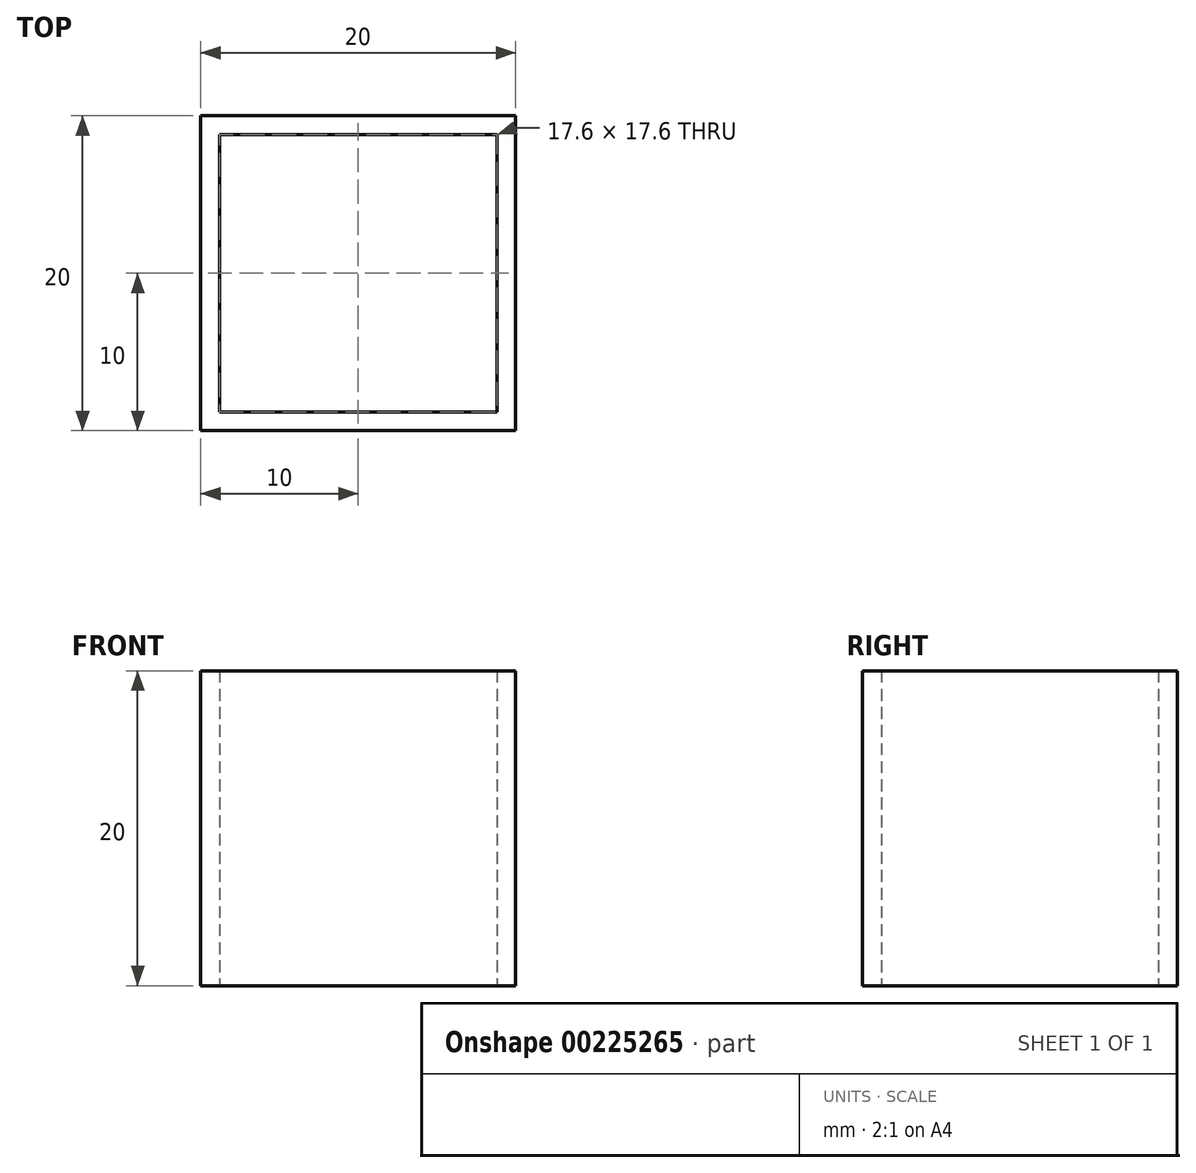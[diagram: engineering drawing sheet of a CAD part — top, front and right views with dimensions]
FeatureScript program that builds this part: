
annotation { "Feature Type Name" : "Feature", "Feature Type Description" : "" }
export const myFeature = defineFeature(function(context is Context, id is Id, definition is map)
    precondition{}
    {
        {
            var Q0;
            Q0=qCreatedBy(makeId("Top.planeOp"),FACE);
            var sketch = newSketch(context, id + "F0", { "sketchPlane" : qUnion([Q0])});
            skLineSegment(sketch, "E0.bottom", {"start": v(-10, 10) * mm, "end": v(10, 10) * mm});
            skLineSegment(sketch, "E0.top", {"start": v(-10, -10) * mm, "end": v(10, -10) * mm});
            skLineSegment(sketch, "E0.left", {"start": v(-10, 10) * mm, "end": v(-10, -10) * mm});
            skLineSegment(sketch, "E0.right", {"start": v(10, 10) * mm, "end": v(10, -10) * mm});
            skPoint(sketch, "E0.middle", {"position": v(0, 0) * mm});
            skLineSegment(sketch, "E1.bottom", {"start": v(-8.8, 8.8) * mm, "end": v(8.8, 8.8) * mm});
            skLineSegment(sketch, "E1.top", {"start": v(-8.8, -8.8) * mm, "end": v(8.8, -8.8) * mm});
            skLineSegment(sketch, "E1.left", {"start": v(-8.8, 8.8) * mm, "end": v(-8.8, -8.8) * mm});
            skLineSegment(sketch, "E1.right", {"start": v(8.8, 8.8) * mm, "end": v(8.8, -8.8) * mm});
            skSolve(sketch);
        }
        {
            var Q0;
            Q0 = qSketchRegion(id + "F0", true);
            extrude(context, id + "F1", {"entities" : qUnion([Q0]), "depth" : 20 * mm, "offsetDistance" : 25 * mm});
        }
    });
